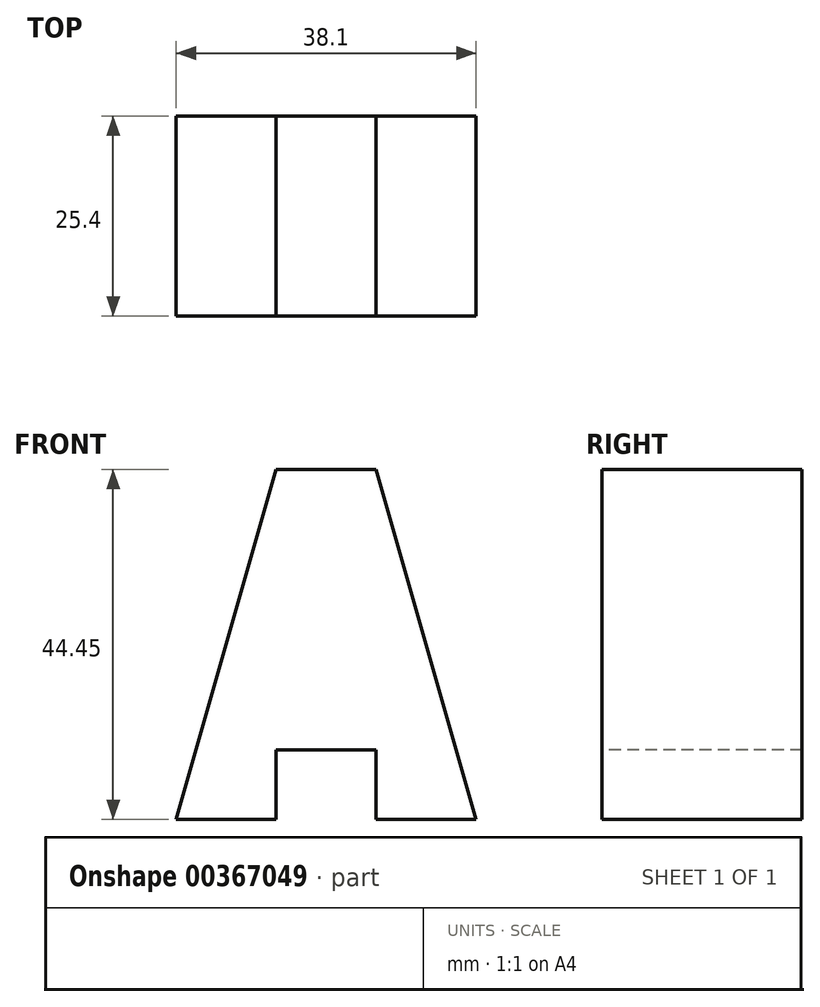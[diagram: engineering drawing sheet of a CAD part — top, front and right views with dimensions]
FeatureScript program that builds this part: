
annotation { "Feature Type Name" : "Feature", "Feature Type Description" : "" }
export const myFeature = defineFeature(function(context is Context, id is Id, definition is map)
    precondition{}
    {
        {
            var Q0;
            Q0=qCreatedBy(makeId("Front.planeOp"),FACE);
            var sketch = newSketch(context, id + "F0", { "sketchPlane" : qUnion([Q0])});
            skLineSegment(sketch, "E0", {"start": v(0, 0) * mm, "end": v(0, 44.45) * mm});
            skLineSegment(sketch, "E1", {"start": v(0, 44.45) * mm, "end": v(38.1, 44.45) * mm});
            skLineSegment(sketch, "E2", {"start": v(38.1, 44.45) * mm, "end": v(38.1, 0) * mm});
            skLineSegment(sketch, "E3", {"start": v(38.1, 0) * mm, "end": v(0, 0) * mm});
            skSolve(sketch);
        }
        {
            var Q0;
            Q0 = qSketchRegion(id + "F0", true);
            extrude(context, id + "F1", {"entities" : qUnion([Q0]), "depth" : 25.4 * mm});
        }
        {
            var Q0;
            Q0=makeQuery(id+"F1.opExtrude","CAP_FACE",FACE,{"disambiguationData":[OSD([sQuery(id+"F0.wireOp",EDGE,"E0"),sQuery(id+"F0.wireOp",EDGE,"E1"),sQuery(id+"F0.wireOp",EDGE,"E2"),sQuery(id+"F0.wireOp",EDGE,"E3")])],"isStart":false});
            var sketch = newSketch(context, id + "F2", { "sketchPlane" : qUnion([Q0])});
            skLineSegment(sketch, "E4", {"start": v(0, 0) * mm, "end": v(12.7, 44.45) * mm});
            skLineSegment(sketch, "E5", {"start": v(12.7, 44.45) * mm, "end": v(25.4, 44.45) * mm});
            skLineSegment(sketch, "E6", {"start": v(25.4, 44.45) * mm, "end": v(38.1, 0) * mm});
            skLineSegment(sketch, "E7", {"start": v(38.1, 0) * mm, "end": v(25.4, 0) * mm});
            skLineSegment(sketch, "E8", {"start": v(25.4, 0) * mm, "end": v(25.4, 8.82) * mm});
            skLineSegment(sketch, "E9", {"start": v(25.4, 8.82) * mm, "end": v(12.7, 8.82) * mm});
            skLineSegment(sketch, "E10", {"start": v(12.7, 8.82) * mm, "end": v(12.7, 0) * mm});
            skLineSegment(sketch, "E11", {"start": v(12.7, 0) * mm, "end": v(0, 0) * mm});
            skSolve(sketch);
        }
        {
            var Q0;
            {var subQ0=sQuery(id+"F2.wireOp",EDGE,"E8");Q0=makeQuery(id+"F2.imprint","IMPRINT",FACE,{"disambiguationData":[TD([[makeQuery(id+"F2.imprint","IMPRINT",EDGE,{"derivedFrom":subQ0}),1.0]])]});}
            var Q1;
            {var subQ0=sQuery(id+"F2.wireOp",EDGE,"E4");Q1=makeQuery(id+"F2.imprint","IMPRINT",FACE,{"disambiguationData":[TD([[makeQuery(id+"F2.imprint","IMPRINT",EDGE,{"derivedFrom":subQ0}),1.0]])]});}
            var Q2;
            {var subQ0=sQuery(id+"F2.wireOp",EDGE,"E6");Q2=makeQuery(id+"F2.imprint","IMPRINT",FACE,{"disambiguationData":[TD([[makeQuery(id+"F2.imprint","IMPRINT",EDGE,{"derivedFrom":subQ0}),1.0]])]});}
            extrude(context, id + "F3", {"entities" : qUnion([Q0, Q1, Q2]), "operationType" : NewBodyOperationType.REMOVE, "oppositeDirection" : true, "depth" : 25.4 * mm});
        }
    });
